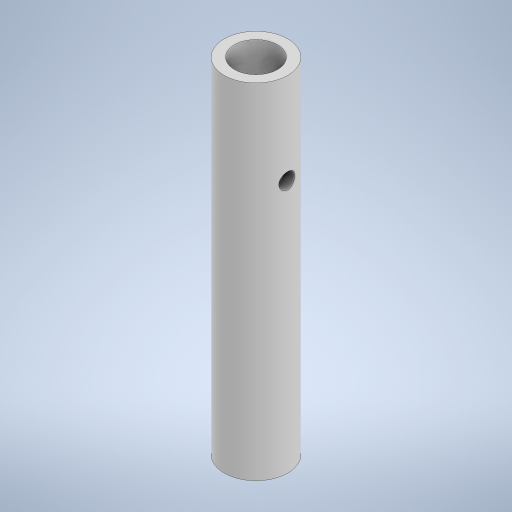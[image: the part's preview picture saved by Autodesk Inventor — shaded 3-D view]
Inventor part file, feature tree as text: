
AUTODESK INVENTOR PART (.ipt)
format: ipt  version: 2023 (Build 270158000, 158)  size: 259,584 bytes
history: native  units: in
note: dims shown in document units (in); Inventor stores cm internally (conversion verified against a paired STEP export)
features: extrude x3, sketch x2
ambient origin geometry x8: Origin, YZ Plane, XZ Plane, XY Plane, X Axis, Y Axis, Z Axis, Center Point
bodies: Solid1 (feature_tree)
feature tree (5):
  extrude  "Extrusion1"  Depth=0.125in
  sketch  "Sketch2"  dims[d2=0.68in d3=0.0in d4=0.066in d5=0.38in d6=0.68in d7=0.0in d8=0.0312in d9=0.18in d10=1.0in d11=0.0in]
  extrude  "Extrusion2"  Depth=0.066in
  extrude  "Extrusion3"  Depth=0.38in
  sketch  "Sketch1"  dims[d0=0.085in d1=0.125in]
